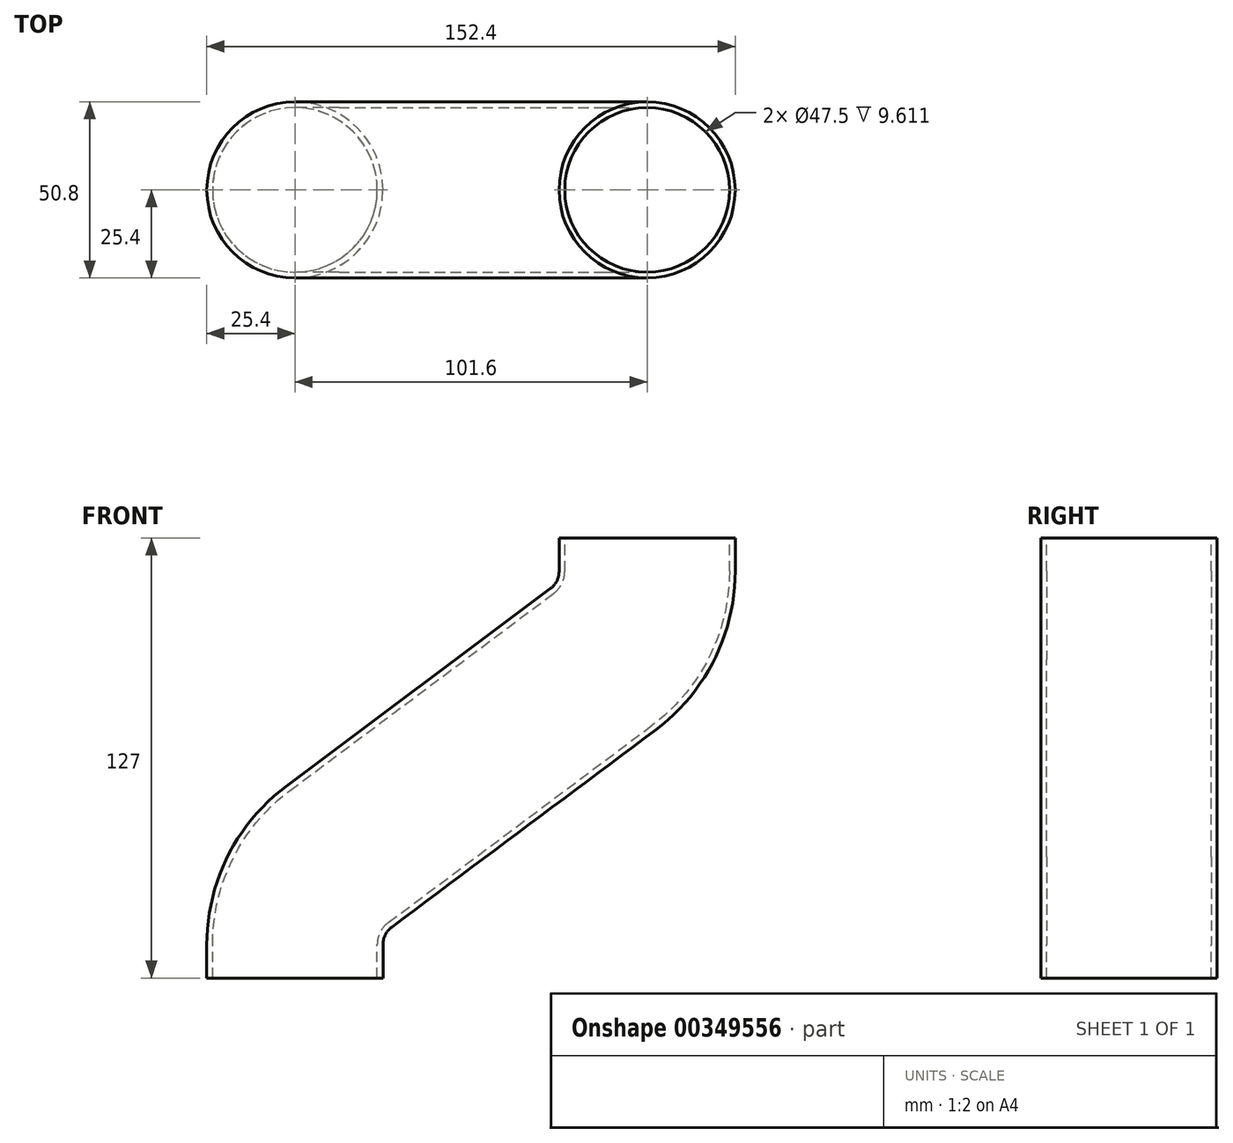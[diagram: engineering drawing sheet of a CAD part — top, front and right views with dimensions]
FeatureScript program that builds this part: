
annotation { "Feature Type Name" : "Feature", "Feature Type Description" : "" }
export const myFeature = defineFeature(function(context is Context, id is Id, definition is map)
    precondition{}
    {
        {
            var Q0;
            Q0=qCreatedBy(makeId("Front.planeOp"),FACE);
            var sketch = newSketch(context, id + "F0", { "sketchPlane" : qUnion([Q0])});
            skLineSegment(sketch, "E0", {"start": v(0, 0) * mm, "end": v(0, 9.61) * mm});
            skLineSegment(sketch, "E1", {"start": v(12.74, 35.04) * mm, "end": v(88.86, 91.96) * mm});
            skLineSegment(sketch, "E2", {"start": v(101.6, 117.39) * mm, "end": v(101.6, 127) * mm});
            skPoint(sketch, "E3.visualSharp", {"position": v(101.6, 101.49) * mm});
            skArc(sketch, "E3.filletArc", {"start": v(88.86, 91.96) * mm, "mid": v(98.24, 103.17) * mm, "end": v(101.6, 117.39) * mm});
            skPoint(sketch, "E4.visualSharp", {"position": v(0, 25.51) * mm});
            skArc(sketch, "E4.filletArc", {"start": v(12.74, 35.04) * mm, "mid": v(3.36, 23.83) * mm, "end": v(0, 9.61) * mm});
            skSolve(sketch);
        }
        {
            var Q0;
            Q0=qCreatedBy(makeId("Top.planeOp"),FACE);
            var sketch = newSketch(context, id + "F1", { "sketchPlane" : qUnion([Q0])});
            skCircle(sketch, "E5", {"center": v(0, 0) * mm, "radius": 25.4 * mm});
            skSolve(sketch);
        }
        {
            var Q0;
            Q0 = qSketchRegion(id + "F1", true);
            var Q1;
            Q1 = qBodyType(qCreatedBy(id + "F1" ,EDGE), BodyType.WIRE);
            var Q2;
            Q2 = qBodyType(qCreatedBy(id + "F0" ,EDGE), BodyType.WIRE);
            sweep(context, id + "F2", {"profiles" : qUnion([Q0]), "surfaceProfiles" : qUnion([Q1]), "path" : qUnion([Q2])});
        }
        {
            var Q0;
            Q0=makeQuery(id+"F2.opSweep","CAP_FACE",FACE,{"disambiguationData":[OSD([sQuery(id+"F0.wireOp",VERTEX,"E0.start"),sQuery(id+"F1.wireOp",EDGE,"E5")])],"isStart":true});
            var sketch = newSketch(context, id + "F3", { "sketchPlane" : qUnion([Q0])});
            skCircle(sketch, "E6", {"center": v(0, 0) * mm, "radius": 23.75 * mm});
            skSolve(sketch);
        }
        {
            var Q0;
            Q0=makeQuery(id+"F3.imprint","IMPRINT",FACE,{"disambiguationData":[TD([[makeQuery(id+"F3.imprint","IMPRINT",EDGE,{"derivedFrom":sQuery(id+"F3.wireOp",EDGE,"E6")}),1.0]])]});
            var Q1;
            Q1 = qBodyType(qCreatedBy(id + "F0" ,EDGE), BodyType.WIRE);
            sweep(context, id + "F4", {"operationType" : NewBodyOperationType.REMOVE, "profiles" : qUnion([Q0]), "path" : qUnion([Q1])});
        }
    });
